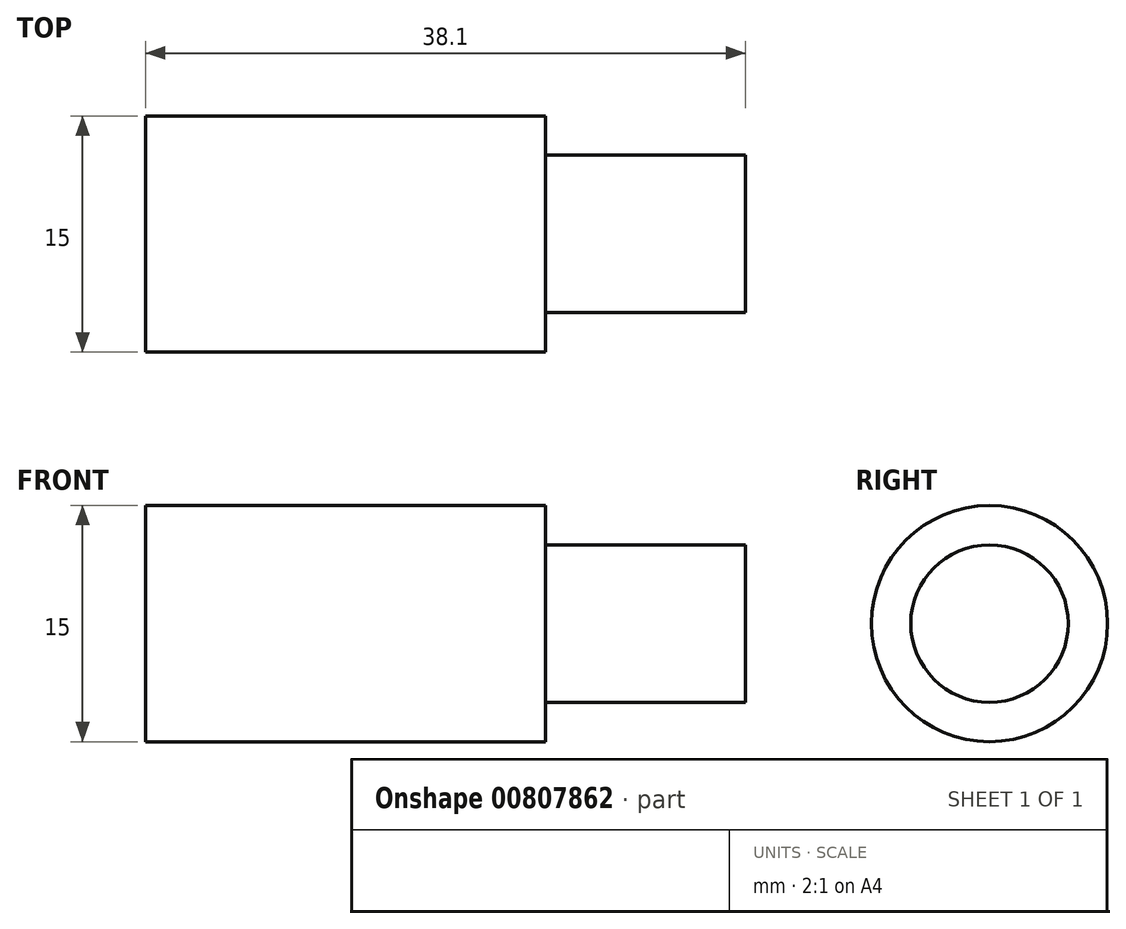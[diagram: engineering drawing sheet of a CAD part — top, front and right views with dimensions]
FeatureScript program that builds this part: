
annotation { "Feature Type Name" : "Feature", "Feature Type Description" : "" }
export const myFeature = defineFeature(function(context is Context, id is Id, definition is map)
    precondition{}
    {
        {
            var Q0;
            Q0=qCreatedBy(makeId("Right.planeOp"),FACE);
            var sketch = newSketch(context, id + "F0", { "sketchPlane" : qUnion([Q0])});
            skCircle(sketch, "E0", {"center": v(0, 0) * mm, "radius": 5 * mm});
            skSolve(sketch);
        }
        {
            var Q0;
            Q0=qCreatedBy(makeId("Right.planeOp"),FACE);
            var sketch = newSketch(context, id + "F1", { "sketchPlane" : qUnion([Q0])});
            skCircle(sketch, "E1", {"center": v(0, 0) * mm, "radius": 7.5 * mm});
            skSolve(sketch);
        }
        {
            var Q0;
            Q0 = qSketchRegion(id + "F0", true);
            extrude(context, id + "F2", {"entities" : qUnion([Q0]), "depth" : 38.1 * mm, "offsetDistance" : 25.4 * mm});
        }
        {
            var Q0;
            Q0=makeQuery(id+"F1.imprint","IMPRINT",FACE,{"disambiguationData":[TD([[makeQuery(id+"F1.imprint","IMPRINT",EDGE,{"derivedFrom":sQuery(id+"F1.wireOp",EDGE,"E1")}),1.0]])]});
            extrude(context, id + "F3", {"entities" : qUnion([Q0]), "operationType" : NewBodyOperationType.ADD, "depth" : 25.4 * mm, "offsetDistance" : 25.4 * mm});
        }
    });
